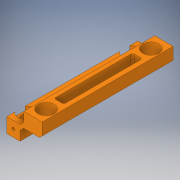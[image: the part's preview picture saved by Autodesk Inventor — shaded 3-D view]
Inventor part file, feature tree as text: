
AUTODESK INVENTOR PART (.ipt)
format: ipt  version: 2019 (Build 230136000, 136)  size: 242,688 bytes
history: native  units: in
note: dims shown in document units (in); Inventor stores cm internally (conversion verified against a paired STEP export)
features: sketch x8, extrude x5, hole x3, chamfer x2, fillet x1, projected_geometry x1
ambient origin geometry x8: Origin, YZ Plane, XZ Plane, XY Plane, X Axis, Y Axis, Z Axis, Center Point
bodies: Solid1 (feature_tree)
feature tree (20):
  extrude  "Extrusion1"  Depth=0.65in
  hole  "Hole2"  [1 undecoded]
  hole  "Hole3"  [1 undecoded]
  extrude  "Extrusion2"  Depth=0.25in
  extrude  "Extrusion3"  Depth=0.35in
  fillet  "Fillet1"  Radius=0.5in
  chamfer  "Chamfer1"  Distance=0.565in
  extrude  "Extrusion4"  Depth=0.7in
  extrude  "Extrusion5"  Depth=0.5in
  chamfer  "Chamfer2"  Distance=1.0in
  hole  "Hole4"  [1 undecoded]
  sketch  "Sketch1"  dims[d0=0.565in d2=0.65in]
  sketch  "Sketch3"  dims[d6=0.7in d9=0.85in]
  sketch  "Sketch4"  dims[d10=5.0in d11=0.0in d25=0.5in]
  sketch  "Sketch5"  dims[d26=0.5in d27=0.25in]
  sketch  "Sketch6"  dims[d28=0.25in]
  sketch  "Sketch7"  dims[d29=0.375in d30=0.75in d31=0.375in d32=0.25in d33=0.5635in d34=1.0in d35=0.8108in d36=0.35in d37=0.5in]
  sketch  "Sketch8"  dims[d38=0.5in]
  sketch  "Sketch9"  dims[d39=0.625in d40=0.75in d41=0.375in d42=0.25in d43=0.5635in d44=1.0in d45=0.8108in d47=0.565in d48=0.7in d49=0.5in d50=1.0in d51=0.175in d52=1.0in d53=0.375in d54=1.0in d55=0.0in d57=0.15in d58=0.15in d59=1.0in d60=0.0in d61=0.075in d62=0.14in d63=0.125in d64=45.0deg d65=0.64in d66=0.64in d67=0.15in d68=0.0in d69=0.15in d70=0.0in d71=0.1in d72=0.125in d73=45.0deg d74=0.565in d75=0.5in d76=0.2825in d77=0.25in d78=0.104in d79=0.75in d80=0.375in d81=0.25in d82=0.5635in d83=1.0in d84=0.8108in d18=1.0in d19=1.0in d20=1.0in d21=0.15in d22=0.25in d23=0.375in d24=0.5635in]
  projected_geometry  "Projected Loop1"
note: 3 required parameter values undecoded (feature->parameter linkage not recoverable at this tier; creation-order binding heuristic only, values carry confidence <= 0.55)
